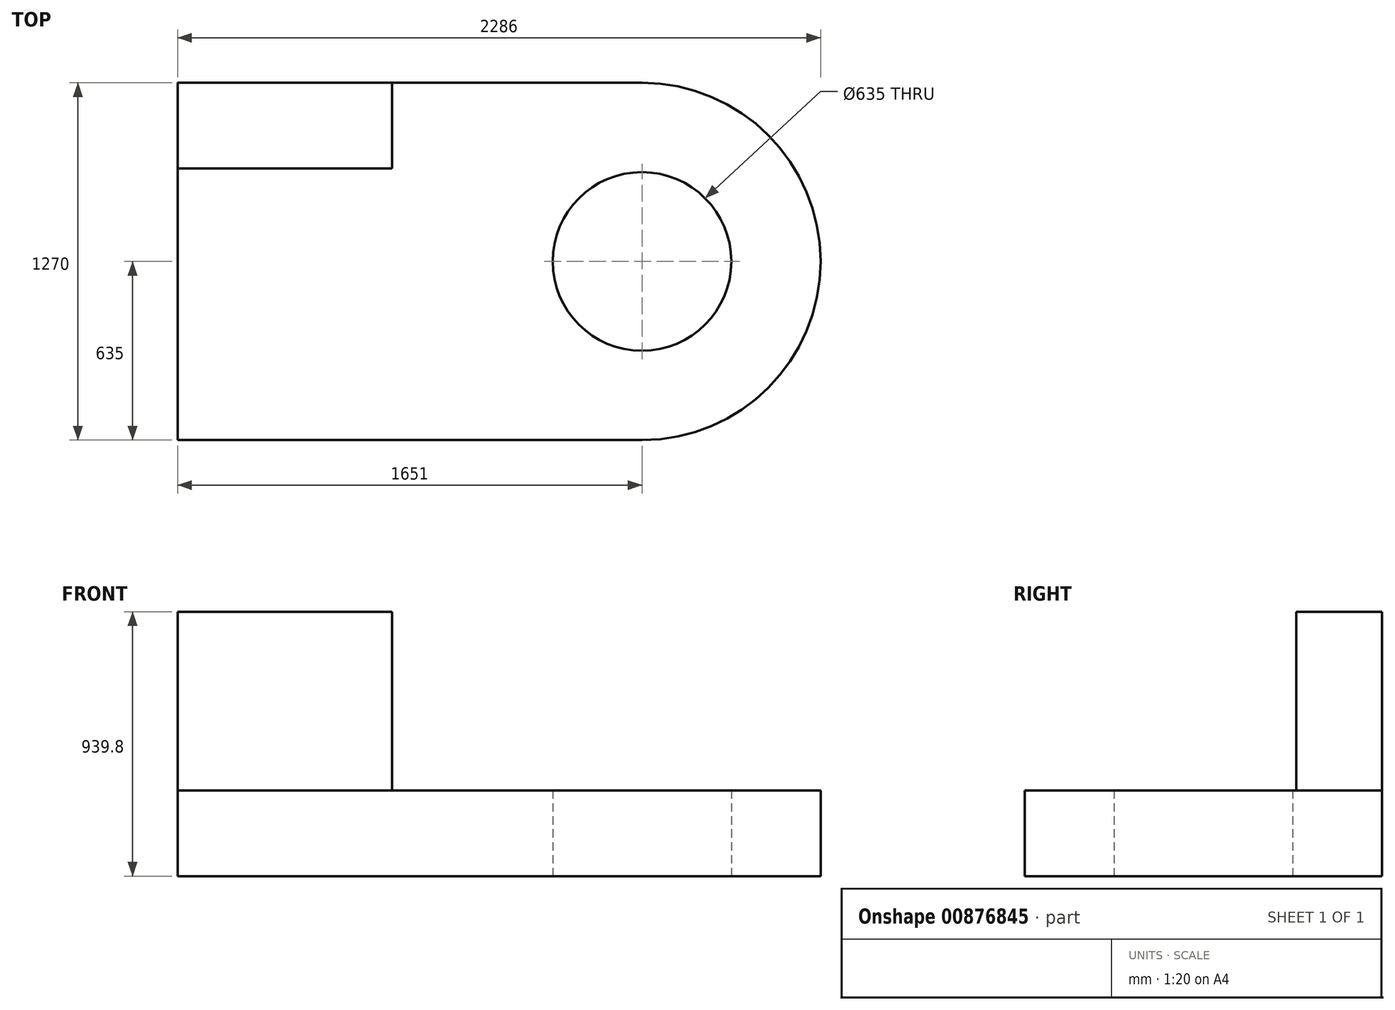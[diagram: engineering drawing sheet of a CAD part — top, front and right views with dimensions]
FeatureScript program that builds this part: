
annotation { "Feature Type Name" : "Feature", "Feature Type Description" : "" }
export const myFeature = defineFeature(function(context is Context, id is Id, definition is map)
    precondition{}
    {
        {
            var Q0;
            Q0=qCreatedBy(makeId("Top.planeOp"),FACE);
            var sketch = newSketch(context, id + "F0", { "sketchPlane" : qUnion([Q0])});
            skLineSegment(sketch, "E0.bottom", {"start": v(825.5, -635) * mm, "end": v(-825.5, -635) * mm});
            skLineSegment(sketch, "E0.top", {"start": v(825.5, 635) * mm, "end": v(-825.5, 635) * mm});
            skLineSegment(sketch, "E0.right", {"start": v(-825.5, -635) * mm, "end": v(-825.5, 635) * mm});
            skPoint(sketch, "E0.middle", {"position": v(0, 0) * mm});
            skArc(sketch, "E1", {"start": v(825.5, -635) * mm, "mid": v(1460.5, 0) * mm, "end": v(825.5, 635) * mm});
            skCircle(sketch, "E2", {"center": v(825.5, 0) * mm, "radius": 317.5 * mm});
            skSolve(sketch);
        }
        {
            var Q0;
            Q0=makeQuery(id+"F0.imprint","IMPRINT",FACE,{"disambiguationData":[TD([[makeQuery(id+"F0.imprint","IMPRINT",EDGE,{"derivedFrom":sQuery(id+"F0.wireOp",EDGE,"E0.bottom")}),-1.0]])]});
            extrude(context, id + "F1", {"entities" : qUnion([Q0]), "depth" : 304.8 * mm, "offsetDistance" : 25.4 * mm});
        }
        {
            var Q0;
            Q0=makeQuery(id+"F1.opExtrude","CAP_FACE",FACE,{"disambiguationData":[OSD([sQuery(id+"F0.wireOp",EDGE,"E0.bottom"),sQuery(id+"F0.wireOp",EDGE,"E0.top"),sQuery(id+"F0.wireOp",EDGE,"E0.right"),sQuery(id+"F0.wireOp",EDGE,"E1"),sQuery(id+"F0.wireOp",EDGE,"E2")])],"isStart":false});
            var sketch = newSketch(context, id + "F2", { "sketchPlane" : qUnion([Q0])});
            skLineSegment(sketch, "E3.bottom", {"start": v(-825.5, 635) * mm, "end": v(-63.5, 635) * mm});
            skLineSegment(sketch, "E3.top", {"start": v(-825.5, 330.2) * mm, "end": v(-63.5, 330.2) * mm});
            skLineSegment(sketch, "E3.left", {"start": v(-825.5, 635) * mm, "end": v(-825.5, 330.2) * mm});
            skLineSegment(sketch, "E3.right", {"start": v(-63.5, 635) * mm, "end": v(-63.5, 330.2) * mm});
            skSolve(sketch);
        }
        {
            var Q0;
            Q0=makeQuery(id+"F2.imprint","IMPRINT",FACE,{"disambiguationData":[TD([[makeQuery(id+"F2.imprint","IMPRINT",EDGE,{"derivedFrom":sQuery(id+"F2.wireOp",EDGE,"E3.bottom")}),1.0]])]});
            extrude(context, id + "F3", {"entities" : qUnion([Q0]), "operationType" : NewBodyOperationType.ADD, "depth" : 635 * mm, "offsetDistance" : 25.4 * mm});
        }
    });
